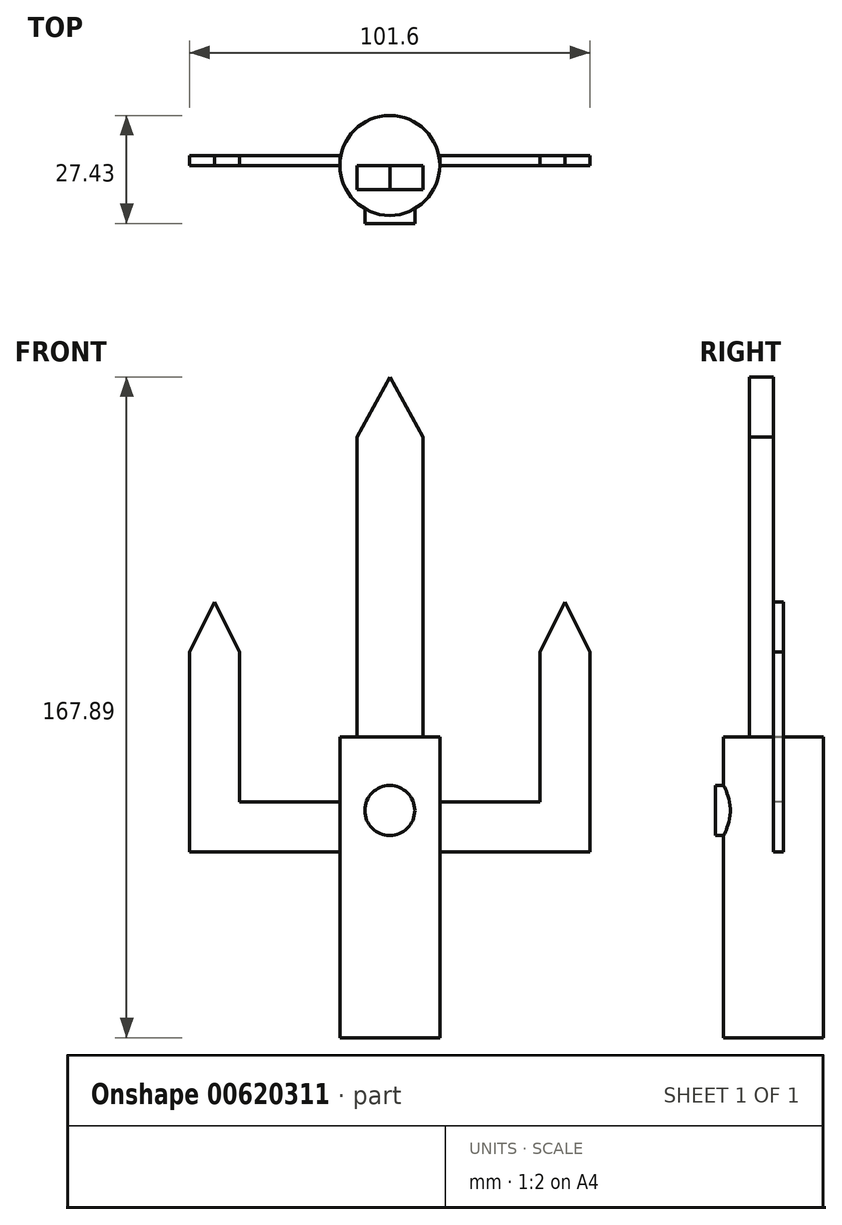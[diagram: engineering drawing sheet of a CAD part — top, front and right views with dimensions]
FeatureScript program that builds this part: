
annotation { "Feature Type Name" : "Feature", "Feature Type Description" : "" }
export const myFeature = defineFeature(function(context is Context, id is Id, definition is map)
    precondition{}
    {
        {
            var Q0;
            Q0=qCreatedBy(makeId("Top.planeOp"),FACE);
            var sketch = newSketch(context, id + "F0", { "sketchPlane" : qUnion([Q0])});
            skCircle(sketch, "E0", {"center": v(0, 0) * mm, "radius": 12.7 * mm});
            skSolve(sketch);
        }
        {
            var Q0;
            Q0 = qSketchRegion(id + "F0", true);
            extrude(context, id + "F1", {"entities" : qUnion([Q0]), "oppositeDirection" : true, "depth" : 76.45 * mm, "offsetDistance" : 25.4 * mm});
        }
        {
            var Q0;
            Q0=qCreatedBy(makeId("Front.planeOp"),FACE);
            var sketch = newSketch(context, id + "F2", { "sketchPlane" : qUnion([Q0])});
            skCircle(sketch, "E1", {"center": v(0, -18.72) * mm, "radius": 6.35 * mm});
            skSolve(sketch);
        }
        {
            var Q0;
            Q0 = qSketchRegion(id + "F2", true);
            extrude(context, id + "F3", {"entities" : qUnion([Q0]), "operationType" : NewBodyOperationType.ADD, "depth" : 14.73 * mm, "offsetDistance" : 25.4 * mm});
        }
        {
            var Q0;
            Q0=qCreatedBy(makeId("Front.planeOp"),FACE);
            var sketch = newSketch(context, id + "F4", { "sketchPlane" : qUnion([Q0])});
            skLineSegment(sketch, "E2", {"start": v(0, 0) * mm, "end": v(0, -76.2) * mm});
            skLineSegment(sketch, "E3", {"start": v(0, -76.2) * mm, "end": v(-12.7, -76.2) * mm});
            skLineSegment(sketch, "E4", {"start": v(-12.7, -76.2) * mm, "end": v(-12.7, -16.5) * mm});
            skLineSegment(sketch, "E5", {"start": v(0, -76.2) * mm, "end": v(12.7, -76.2) * mm});
            skLineSegment(sketch, "E6", {"start": v(12.7, -76.2) * mm, "end": v(12.7, -16.5) * mm});
            skLineSegment(sketch, "E7", {"start": v(12.7, -16.5) * mm, "end": v(38.1, -16.5) * mm});
            skLineSegment(sketch, "E8", {"start": v(38.1, -16.5) * mm, "end": v(38.1, 21.6) * mm});
            skLineSegment(sketch, "E9", {"start": v(38.1, 21.6) * mm, "end": v(50.8, 21.6) * mm});
            skLineSegment(sketch, "E10", {"start": v(12.7, -16.5) * mm, "end": v(12.7, -29.2) * mm});
            skLineSegment(sketch, "E11", {"start": v(12.7, -29.2) * mm, "end": v(50.8, -29.2) * mm});
            skLineSegment(sketch, "E12", {"start": v(50.8, -29.2) * mm, "end": v(50.8, 21.6) * mm});
            skLineSegment(sketch, "E13", {"start": v(44.45, 21.6) * mm, "end": v(44.45, 34.3) * mm});
            skLineSegment(sketch, "E14", {"start": v(44.45, 34.3) * mm, "end": v(50.8, 21.6) * mm});
            skLineSegment(sketch, "E15", {"start": v(44.45, 34.3) * mm, "end": v(38.1, 21.6) * mm});
            skLineSegment(sketch, "E16", {"start": v(-12.7, -16.5) * mm, "end": v(-38.1, -16.5) * mm});
            skLineSegment(sketch, "E17", {"start": v(-38.1, -16.5) * mm, "end": v(-38.1, 21.59) * mm});
            skLineSegment(sketch, "E18", {"start": v(-38.1, 21.59) * mm, "end": v(-50.8, 21.59) * mm});
            skLineSegment(sketch, "E19", {"start": v(-12.7, -16.5) * mm, "end": v(-12.7, -29.21) * mm});
            skLineSegment(sketch, "E20", {"start": v(-12.7, -29.21) * mm, "end": v(-50.8, -29.21) * mm});
            skLineSegment(sketch, "E21", {"start": v(-50.8, -29.21) * mm, "end": v(-50.8, 21.59) * mm});
            skLineSegment(sketch, "E22", {"start": v(-44.45, 21.59) * mm, "end": v(-44.45, 34.3) * mm});
            skLineSegment(sketch, "E23", {"start": v(-44.45, 34.3) * mm, "end": v(-50.8, 21.6) * mm});
            skLineSegment(sketch, "E24", {"start": v(-44.45, 34.3) * mm, "end": v(-38.1, 21.6) * mm});
            skSolve(sketch);
        }
        {
            var Q0;
            Q0 = qSketchRegion(id + "F4", true);
            extrude(context, id + "F5", {"entities" : qUnion([Q0]), "oppositeDirection" : true, "depth" : 2.54 * mm, "offsetDistance" : 25.4 * mm});
        }
        {
            var Q0;
            Q0=qCreatedBy(makeId("Front.planeOp"),FACE);
            var sketch = newSketch(context, id + "F6", { "sketchPlane" : qUnion([Q0])});
            skLineSegment(sketch, "E25", {"start": v(0, 0) * mm, "end": v(-8.38, 0) * mm});
            skLineSegment(sketch, "E26", {"start": v(-8.38, 0) * mm, "end": v(-8.38, 76.2) * mm});
            skLineSegment(sketch, "E27", {"start": v(0, 0) * mm, "end": v(8.38, 0) * mm});
            skLineSegment(sketch, "E28", {"start": v(8.38, 0) * mm, "end": v(8.38, 76.2) * mm});
            skLineSegment(sketch, "E29", {"start": v(8.38, 76.2) * mm, "end": v(-8.38, 76.2) * mm});
            skPoint(sketch, "E30.endSnap0", {"position": v(0, 76.2) * mm});
            skLineSegment(sketch, "E31", {"start": v(0, 76.2) * mm, "end": v(0, 91.44) * mm});
            skLineSegment(sketch, "E32", {"start": v(0, 91.44) * mm, "end": v(-8.38, 76.2) * mm});
            skLineSegment(sketch, "E33", {"start": v(0, 91.44) * mm, "end": v(8.38, 76.2) * mm});
            skSolve(sketch);
        }
        {
            var Q0;
            Q0 = qSketchRegion(id + "F6", true);
            extrude(context, id + "F7", {"entities" : qUnion([Q0]), "operationType" : NewBodyOperationType.ADD, "depth" : 3.56 * mm, "offsetDistance" : 25.4 * mm});
        }
        {
            var Q0;
            Q0 = qSketchRegion(id + "F6", true);
            extrude(context, id + "F8", {"entities" : qUnion([Q0]), "operationType" : NewBodyOperationType.ADD, "depth" : 6.1 * mm, "offsetDistance" : 25.4 * mm});
        }
    });
